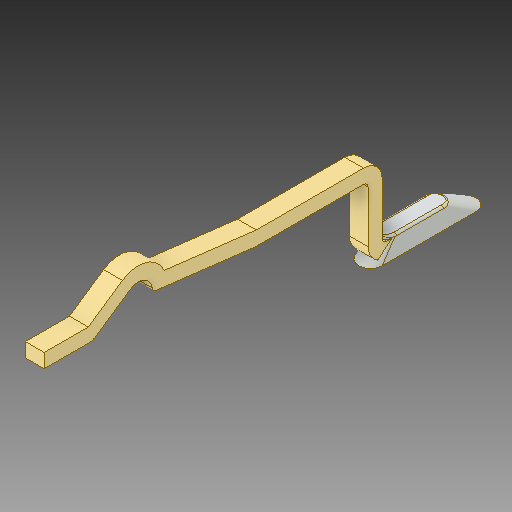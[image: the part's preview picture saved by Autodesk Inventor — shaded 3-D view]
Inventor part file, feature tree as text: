
AUTODESK INVENTOR PART (.ipt)
format: ipt  version: 2019 (Build 230136000, 136)  size: 160,768 bytes
history: native  units: in
note: dims shown in document units (in); Inventor stores cm internally (conversion verified against a paired STEP export)
features: fillet x1
ambient origin geometry x8: Origin, YZ Plane, XZ Plane, XY Plane, X Axis, Y Axis, Z Axis, Center Point
bodies: Solid1 (feature_tree)
feature tree (1):
  fillet  "Fillet2"  [1 undecoded]
note: 1 required parameter value undecoded (feature->parameter linkage not recoverable at this tier; creation-order binding heuristic only, values carry confidence <= 0.55)
